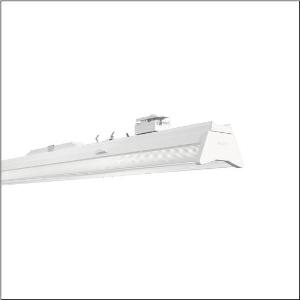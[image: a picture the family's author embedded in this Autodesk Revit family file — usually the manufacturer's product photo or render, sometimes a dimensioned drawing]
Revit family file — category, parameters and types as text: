
# Revit family: licross_21_performance_mo_52tm167n485g
name_source: partatom
category: Lighting Fixtures
units: mm (PartAtom-declared; Revit-internal decimal feet)

## family parameters
Cut with Voids When Loaded = No
Host = Face
Light Source = No
Part Type = Normal
Room Calculation Point = No
Round Connector Dimension = Use Diameter
Shared = No

## types (1)
- Licross 21 Performance MO (1 x LED, 8720 lm, 47.9 W, 4000K)
    Apparent Load = 48 VA
    CIE Flux Codes = 66 88 96 79 100
    Color Rendering = 80
    Color Temperature = 4000K
    Default Elevation = 1800 mm
    Description = Licross 21 Performance MO, luminaire insert, of sheet steel, galvanised, coil coated, white, length: 1.500mm, width: 120mm, height: 123mm, LED rated luminous flux: 8.720lm, light colour: 840, SDCM (Standard Deviation of Colour Matching)MacAdam ≤ 3 SDCM (initial), control gear: ON/OFF, with plug, 3-pole, with phase selection, mains connection: 220..240V, AC, 50/60Hz, rated input power: 48W, internal wiring halogen-free, primary light control with lens, of plastic, primary optical cover: cover, of PMMA, light emission: direct/indirect distribution, primary light characteristic: symmetric, protection rating (complete): IP40, insulation class (complete): insulation class I (protective earthing), certification: CE, ENEC, UKCA, protection symbol: D if used in an environment without relevant dust loads with corresponding accessories, impact resistance: IK06, permissible ambient temperature for indoor applications: -35..+45°C, corresponds to IFS (International Featured Standards) requirements for safety and quality in the food industry, reducing of maximum allowable ambient temperature of 5°C with ceiling mounting, LABS conformity tested according to VDMA 24364:2018-05, The light source and the operating device comply with the requirements of the Ecodesign Regulation (EU) 2019/2020 and are replaceable in accordance with this regulation, packaging unit: 1 piece
    Height = 114 mm
    Lamp = 1 x LED
    Lamp Light Flux = 8720 lm
    Lamp Power = 47.9 W
    Lamp count = 1
    Length = 1500 mm
    Luminous efficacy = 182 lm/W
    Manufacturer = Siteco
    ModVariant = No
    Model = 52TM167N485G
    Mounting Place = Ceiling
    Mounting Type = Pendant
    Number of Poles = 1
    OnlyDefault = Yes
    Power Factor = 1
    Product Name = Licross 21 Performance MO
    Product group = luminaire insert | ceiling pendant
    ProductGroupID = 901
    Protection Class = Protection class I
    Protection Degree = IP 40
    RLX_Detail_Level = 1
    RLX_Emergency_Light_Flux = 0 lm
    RLX_Emergency_Type = 0
    RLX_Emergency_Type_DB = No
    RlxData = <blob elided: 30645 chars, md5=b68639f4>
    Socket = socket
    Standby Power = 0 W
    System Light Flux = 8720 lm
    System Power = 48 W
    Type Comments = Product without accessories
    Type Image = l_1256138.jpg
    URL = http://relux.com
    VarID = ---
    Voltage = 0 V
    Weight = 0.00 kg
    Width = 120 mm

## geometry (parser evidence)
native form markers: Blend x4, Sweep x11
no freeform markers — native parametric forms only
